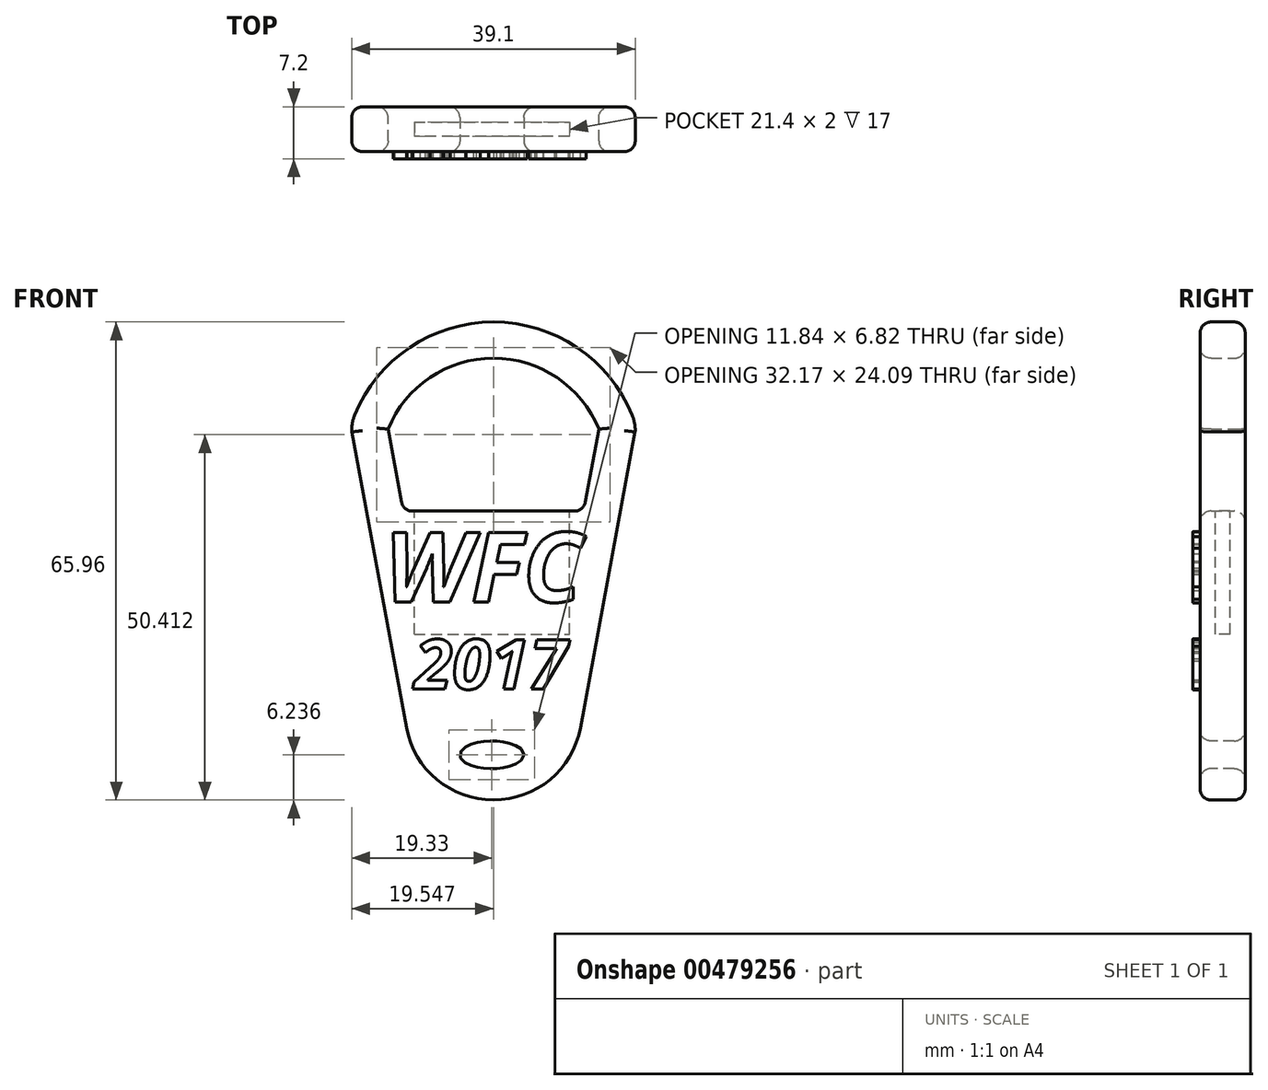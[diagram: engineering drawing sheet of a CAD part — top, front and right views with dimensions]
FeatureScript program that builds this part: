
annotation { "Feature Type Name" : "Feature", "Feature Type Description" : "" }
export const myFeature = defineFeature(function(context is Context, id is Id, definition is map)
    precondition{}
    {
        {
            var Q0;
            Q0=qCreatedBy(makeId("Front.planeOp"),FACE);
            var sketch = newSketch(context, id + "F0", { "sketchPlane" : qUnion([Q0])});
            skLineSegment(sketch, "E0", {"start": v(0.22, 53.5) * mm, "end": v(0.22, -27.22) * mm, "construction": true});
            skLineSegment(sketch, "E1", {"start": v(19.76, 12.33) * mm, "end": v(12.22, -28.48) * mm});
            skLineSegment(sketch, "E2.MirrorCS", {"start": v(-19.33, 12.33) * mm, "end": v(-11.78, -28.48) * mm});
            skLineSegment(sketch, "E3.0", {"start": v(-14.31, 12.71) * mm, "end": v(-12.22, 1.4) * mm});
            skLineSegment(sketch, "E3.3", {"start": v(14.75, 12.71) * mm, "end": v(12.66, 1.4) * mm});
            skLineSegment(sketch, "E4", {"start": v(-12.22, 1.4) * mm, "end": v(12.66, 1.4) * mm});
            skPoint(sketch, "E5", {"position": v(0.22, 20.6) * mm});
            skPoint(sketch, "E6", {"position": v(-14.31, 12.71) * mm});
            skPoint(sketch, "E7.MirrorP", {"position": v(14.75, 12.71) * mm});
            skArc(sketch, "E8", {"start": v(14.75, 12.71) * mm, "mid": v(0.22, 22.5) * mm, "end": v(-14.31, 12.71) * mm});
            skArc(sketch, "E9.0", {"start": v(19.62, 13.97) * mm, "mid": v(0.56, 27.5) * mm, "end": v(-18.94, 14.6) * mm});
            skArc(sketch, "E10", {"start": v(-18.94, 14.6) * mm, "mid": v(-19.26, 13.5) * mm, "end": v(-19.33, 12.33) * mm});
            skArc(sketch, "E11.MirrorCS", {"start": v(19.38, 14.6) * mm, "mid": v(19.7, 13.5) * mm, "end": v(19.76, 12.33) * mm});
            skPoint(sketch, "E12.orphan", {"position": v(-21.9, 26.19) * mm});
            skPoint(sketch, "E13.orphan", {"position": v(22.32, 26.19) * mm});
            skPoint(sketch, "E14.MirrorCS.start.orphan", {"position": v(0.22, 25.6) * mm});
            skArc(sketch, "E15", {"start": v(-11.78, -28.48) * mm, "mid": v(0.22, -38.46) * mm, "end": v(12.22, -28.48) * mm});
            skPoint(sketch, "E16.MirrorCS.end.orphan", {"position": v(0.22, -28.48) * mm});
            skPoint(sketch, "E16.MirrorCS.start.orphan", {"position": v(-11.78, -28.48) * mm});
            skLineSegment(sketch, "E17", {"start": v(-11.78, -28.48) * mm, "end": v(12.22, -28.48) * mm, "construction": true});
            skSolve(sketch);
        }
        {
            var Q0;
            Q0=qSketchRegion(id+"F0",true);
            extrude(context, id + "F1", {"entities" : qUnion([Q0]), "depth" : 6.2 * mm});
        }
        {
            var Q0;
            Q0=makeQuery(id+"F1.opExtrude","CAP_FACE",FACE,{"disambiguationData":[OSD([sQuery(id+"F0.wireOp",EDGE,"E1"),sQuery(id+"F0.wireOp",EDGE,"E2.MirrorCS"),sQuery(id+"F0.wireOp",EDGE,"E3.0"),sQuery(id+"F0.wireOp",EDGE,"E3.3"),sQuery(id+"F0.wireOp",EDGE,"E4"),sQuery(id+"F0.wireOp",EDGE,"E8"),sQuery(id+"F0.wireOp",EDGE,"E9.0"),sQuery(id+"F0.wireOp",EDGE,"E10"),sQuery(id+"F0.wireOp",EDGE,"E11.MirrorCS"),sQuery(id+"F0.wireOp",EDGE,"E15")])],"isStart":false});
            var sketch = newSketch(context, id + "F2", { "sketchPlane" : qUnion([Q0])});
            skEllipse(sketch, "E18", {"center": v(0, -32.22) * mm, "majorRadius": 4.42 * mm, "minorRadius": 1.9 * mm, "majorAxis": v(1, 0)});
            skSolve(sketch);
        }
        {
            var Q0;
            Q0=makeQuery(id+"F2.imprint","IMPRINT",FACE,{"disambiguationData":[TD([[makeQuery(id+"F2.imprint","IMPRINT",EDGE,{"derivedFrom":sQuery(id+"F2.wireOp",EDGE,"E18")}),1.0]])]});
            extrude(context, id + "F3", {"entities" : qUnion([Q0]), "operationType" : NewBodyOperationType.REMOVE, "oppositeDirection" : true, "depth" : 6.5 * mm});
        }
        {
            var Q0;
            Q0=makeQuery(id+"F1.opExtrude","SWEPT_FACE",FACE,{"disambiguationData":[OSD([sQuery(id+"F0.wireOp",EDGE,"E4")])]});
            var sketch = newSketch(context, id + "F4", { "sketchPlane" : qUnion([Q0])});
            skLineSegment(sketch, "E19", {"start": v(0, -2.1) * mm, "end": v(10.7, -2.1) * mm});
            skLineSegment(sketch, "E20.0", {"start": v(0, -4.1) * mm, "end": v(10.7, -4.1) * mm});
            skLineSegment(sketch, "E21", {"start": v(10.7, -2.1) * mm, "end": v(10.7, -4.1) * mm});
            skLineSegment(sketch, "E22", {"start": v(0, -2.1) * mm, "end": v(0, -4.1) * mm, "construction": true});
            skLineSegment(sketch, "E23.MirrorCS", {"start": v(0, -2.1) * mm, "end": v(-10.7, -2.1) * mm});
            skLineSegment(sketch, "E24.MirrorCS", {"start": v(-10.7, -2.1) * mm, "end": v(-10.7, -4.1) * mm});
            skLineSegment(sketch, "E25.MirrorCS", {"start": v(0, -4.1) * mm, "end": v(-10.7, -4.1) * mm});
            skSolve(sketch);
        }
        {
            var Q0;
            Q0=makeQuery(id+"F4.imprint","IMPRINT",FACE,{"disambiguationData":[TD([[makeQuery(id+"F4.imprint","IMPRINT",EDGE,{"derivedFrom":sQuery(id+"F4.wireOp",EDGE,"E19")}),-1.0]])]});
            extrude(context, id + "F5", {"entities" : qUnion([Q0]), "operationType" : NewBodyOperationType.REMOVE, "oppositeDirection" : true, "depth" : 17 * mm});
        }
        {
            var Q0;
            Q0=makeQuery(id+"F1.opExtrude","SWEPT_EDGE",EDGE,{"disambiguationData":[OSD([sQuery(id+"F0.wireOp",EDGE,"E3.0"),sQuery(id+"F0.wireOp",EDGE,"E4")])]});
            var Q1;
            Q1=makeQuery(id+"F1.opExtrude","SWEPT_EDGE",EDGE,{"disambiguationData":[OSD([sQuery(id+"F0.wireOp",EDGE,"E3.3"),sQuery(id+"F0.wireOp",EDGE,"E4")])]});
            var Q2;
            Q2=makeQuery(id+"F1.opExtrude","CAP_FACE",FACE,{"disambiguationData":[OSD([sQuery(id+"F0.wireOp",EDGE,"E1"),sQuery(id+"F0.wireOp",EDGE,"E2.MirrorCS"),sQuery(id+"F0.wireOp",EDGE,"E3.0"),sQuery(id+"F0.wireOp",EDGE,"E3.3"),sQuery(id+"F0.wireOp",EDGE,"E4"),sQuery(id+"F0.wireOp",EDGE,"E8"),sQuery(id+"F0.wireOp",EDGE,"E9.0"),sQuery(id+"F0.wireOp",EDGE,"E10"),sQuery(id+"F0.wireOp",EDGE,"E11.MirrorCS"),sQuery(id+"F0.wireOp",EDGE,"E15")])],"isStart":false});
            var Q3;
            Q3=makeQuery(id+"F1.opExtrude","CAP_FACE",FACE,{"disambiguationData":[OSD([sQuery(id+"F0.wireOp",EDGE,"E1"),sQuery(id+"F0.wireOp",EDGE,"E2.MirrorCS"),sQuery(id+"F0.wireOp",EDGE,"E3.0"),sQuery(id+"F0.wireOp",EDGE,"E3.3"),sQuery(id+"F0.wireOp",EDGE,"E4"),sQuery(id+"F0.wireOp",EDGE,"E8"),sQuery(id+"F0.wireOp",EDGE,"E9.0"),sQuery(id+"F0.wireOp",EDGE,"E10"),sQuery(id+"F0.wireOp",EDGE,"E11.MirrorCS"),sQuery(id+"F0.wireOp",EDGE,"E15")])],"isStart":true});
            fillet(context, id + "F6", {"entities" : qUnion([Q0, Q1, Q2, Q3]), "radius" : 1.5 * mm, "tangentPropagation" : true, "allowEdgeOverflow" : false});
        }
        {
            var Q0;
            Q0=makeQuery(id+"F1.opExtrude","CAP_FACE",FACE,{"disambiguationData":[OSD([sQuery(id+"F0.wireOp",EDGE,"E1"),sQuery(id+"F0.wireOp",EDGE,"E2.MirrorCS"),sQuery(id+"F0.wireOp",EDGE,"E3.0"),sQuery(id+"F0.wireOp",EDGE,"E3.3"),sQuery(id+"F0.wireOp",EDGE,"E4"),sQuery(id+"F0.wireOp",EDGE,"E8"),sQuery(id+"F0.wireOp",EDGE,"E9.0"),sQuery(id+"F0.wireOp",EDGE,"E10"),sQuery(id+"F0.wireOp",EDGE,"E11.MirrorCS"),sQuery(id+"F0.wireOp",EDGE,"E15")])],"isStart":false});
            var sketch = newSketch(context, id + "F7", { "sketchPlane" : qUnion([Q0])});
            skText(sketch, "E26", { "text": "2017", "fontName": "OpenSans-BoldItalic.ttf"});
            const initialGuessF7  = {"E26": [-0.01073, -0.02317, 1, 0, 0.0069]};
            skSetInitialGuess(sketch, initialGuessF7);
            skSolve(sketch);
        }
        {
            var Q0;
            Q0 = qSketchRegion(id + "F7", true);
            extrude(context, id + "F8", {"entities" : qUnion([Q0]), "operationType" : NewBodyOperationType.ADD, "depth" : 1 * mm, "offsetDistance" : 25 * mm});
        }
        {
            var Q0;
            {var subQ11=sQuery(id+"F0.wireOp",EDGE,"E10");var subQ13=sQuery(id+"F0.wireOp",EDGE,"E9.0");var subQ23=sQuery(id+"F0.wireOp",EDGE,"E8");var subQ24=sQuery(id+"F0.wireOp",EDGE,"E4");var subQ25=sQuery(id+"F0.wireOp",EDGE,"E3.3");var subQ26=sQuery(id+"F0.wireOp",EDGE,"E3.0");var subQ27=sQuery(id+"F0.wireOp",EDGE,"E15");var subQ28=sQuery(id+"F0.wireOp",EDGE,"E1");var subQ29=sQuery(id+"F0.wireOp",EDGE,"E2.MirrorCS");var subQ30=sQuery(id+"F0.wireOp",EDGE,"E11.MirrorCS");Q0=makeQuery(id+"F8.boolean.opBoolean","SPLIT",FACE,{"disambiguationData":[TD([makeQuery(id+"F6.opFillet","BLEND_FACE",FACE,{"disambiguationData":[OSD([sQuery(id+"F2.wireOp",EDGE,"E18")])]})])],"derivedFrom":makeQuery(id+"F1.opExtrude","CAP_FACE",FACE,{"disambiguationData":[OSD([subQ28,subQ29,subQ26,subQ25,subQ24,subQ23,subQ13,subQ11,subQ30,subQ27])],"isStart":false})});}
            var sketch = newSketch(context, id + "F9", { "sketchPlane" : qUnion([Q0])});
            skText(sketch, "E27", { "text": "WFC", "fontName": "OpenSans-BoldItalic.ttf"});
            const initialGuessF9  = {"E27": [-0.01483, -0.01114, 1, 0, 0.00966]};
            skSetInitialGuess(sketch, initialGuessF9);
            skSolve(sketch);
        }
        {
            var Q0;
            Q0 = qSketchRegion(id + "F9", true);
            extrude(context, id + "F10", {"entities" : qUnion([Q0]), "operationType" : NewBodyOperationType.ADD, "depth" : 1 * mm, "offsetDistance" : 25 * mm});
        }
    });
